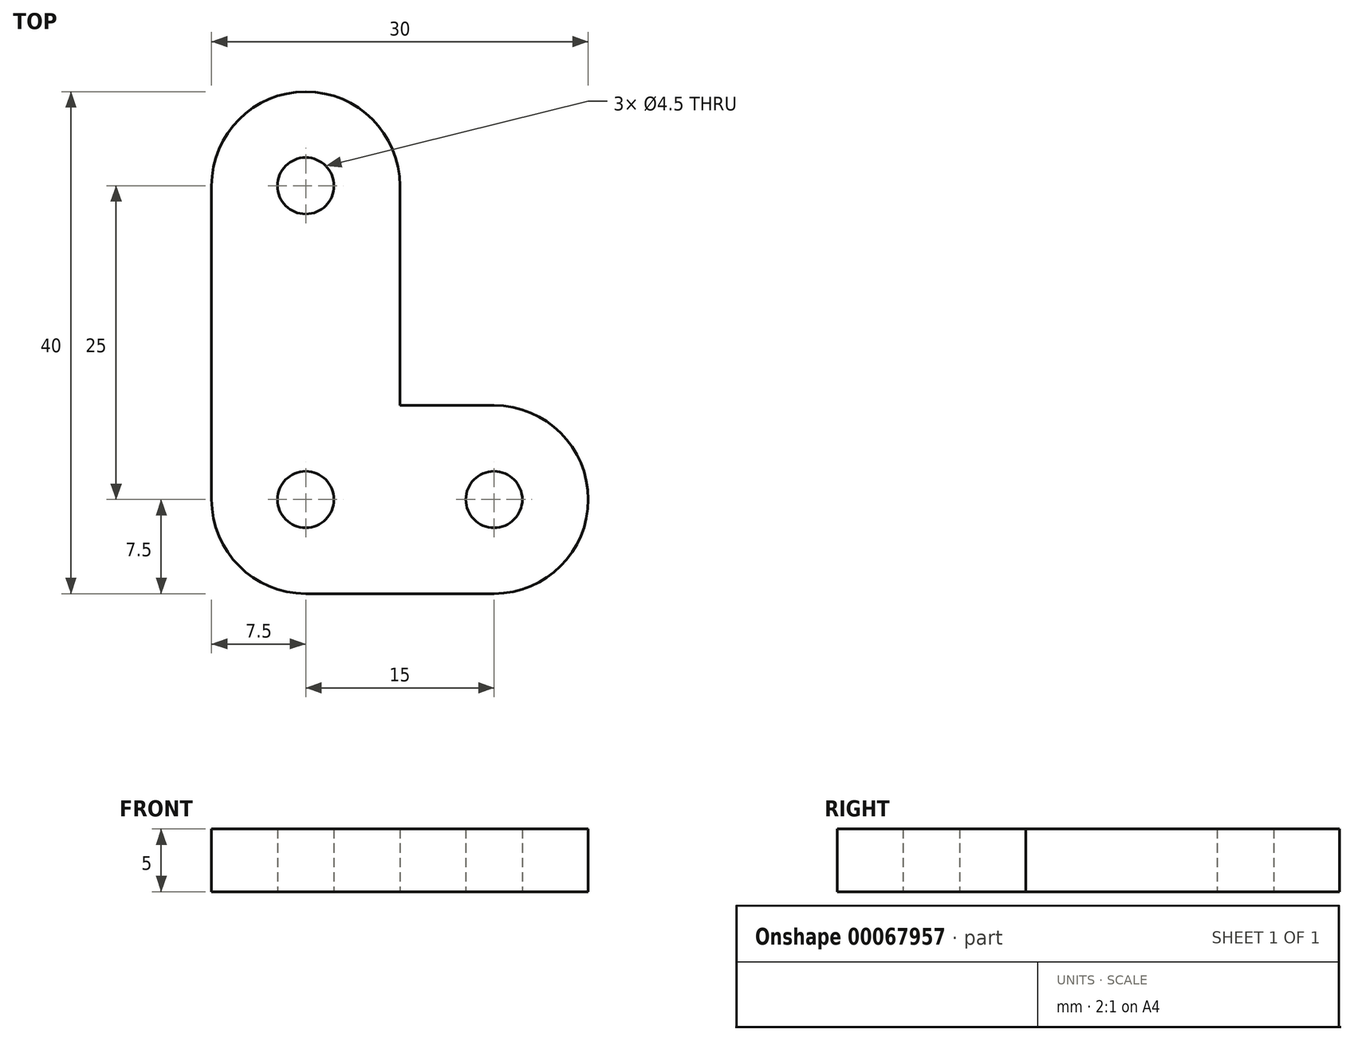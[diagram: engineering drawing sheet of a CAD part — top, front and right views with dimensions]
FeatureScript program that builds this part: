
annotation { "Feature Type Name" : "Feature", "Feature Type Description" : "" }
export const myFeature = defineFeature(function(context is Context, id is Id, definition is map)
    precondition{}
    {
        {
            var Q0;
            Q0=qCreatedBy(makeId("Top.planeOp"),FACE);
            var sketch = newSketch(context, id + "F0", { "sketchPlane" : qUnion([Q0])});
            skLineSegment(sketch, "E0", {"start": v(0, 25) * mm, "end": v(0, 25) * mm});
            skLineSegment(sketch, "E1", {"start": v(-7.5, 17.5) * mm, "end": v(-7.5, -7.5) * mm});
            skLineSegment(sketch, "E2", {"start": v(0, -15) * mm, "end": v(15, -15) * mm});
            skLineSegment(sketch, "E3", {"start": v(22.5, -7.5) * mm, "end": v(22.5, -7.5) * mm});
            skLineSegment(sketch, "E4", {"start": v(15, 0) * mm, "end": v(7.5, 0) * mm});
            skLineSegment(sketch, "E5", {"start": v(7.5, 0) * mm, "end": v(7.5, 17.5) * mm});
            skCircle(sketch, "E6", {"center": v(0, 17.5) * mm, "radius": 2.25 * mm});
            skCircle(sketch, "E7", {"center": v(0, -7.5) * mm, "radius": 2.25 * mm});
            skCircle(sketch, "E8", {"center": v(15, -7.5) * mm, "radius": 2.25 * mm});
            skPoint(sketch, "E9.visualSharp", {"position": v(-7.5, 25) * mm});
            skArc(sketch, "E9.filletArc", {"start": v(0, 25) * mm, "mid": v(-5.3, 22.8) * mm, "end": v(-7.5, 17.5) * mm});
            skPoint(sketch, "E10.visualSharp", {"position": v(7.5, 25) * mm});
            skArc(sketch, "E10.filletArc", {"start": v(7.5, 17.5) * mm, "mid": v(5.3, 22.8) * mm, "end": v(0, 25) * mm});
            skPoint(sketch, "E11.visualSharp", {"position": v(22.5, 0) * mm});
            skArc(sketch, "E11.filletArc", {"start": v(22.5, -7.5) * mm, "mid": v(20.3, -2.2) * mm, "end": v(15, 0) * mm});
            skPoint(sketch, "E12.visualSharp", {"position": v(22.5, -15) * mm});
            skArc(sketch, "E12.filletArc", {"start": v(15, -15) * mm, "mid": v(20.3, -12.8) * mm, "end": v(22.5, -7.5) * mm});
            skPoint(sketch, "E13.visualSharp", {"position": v(-7.5, -15) * mm});
            skArc(sketch, "E13.filletArc", {"start": v(-7.5, -7.5) * mm, "mid": v(-5.3, -12.8) * mm, "end": v(0, -15) * mm});
            skSolve(sketch);
        }
        {
            var Q0;
            Q0=qSketchRegion(id+"F0",true);
            extrude(context, id + "F1", {"entities" : qUnion([Q0]), "depth" : 5 * mm});
        }
    });
